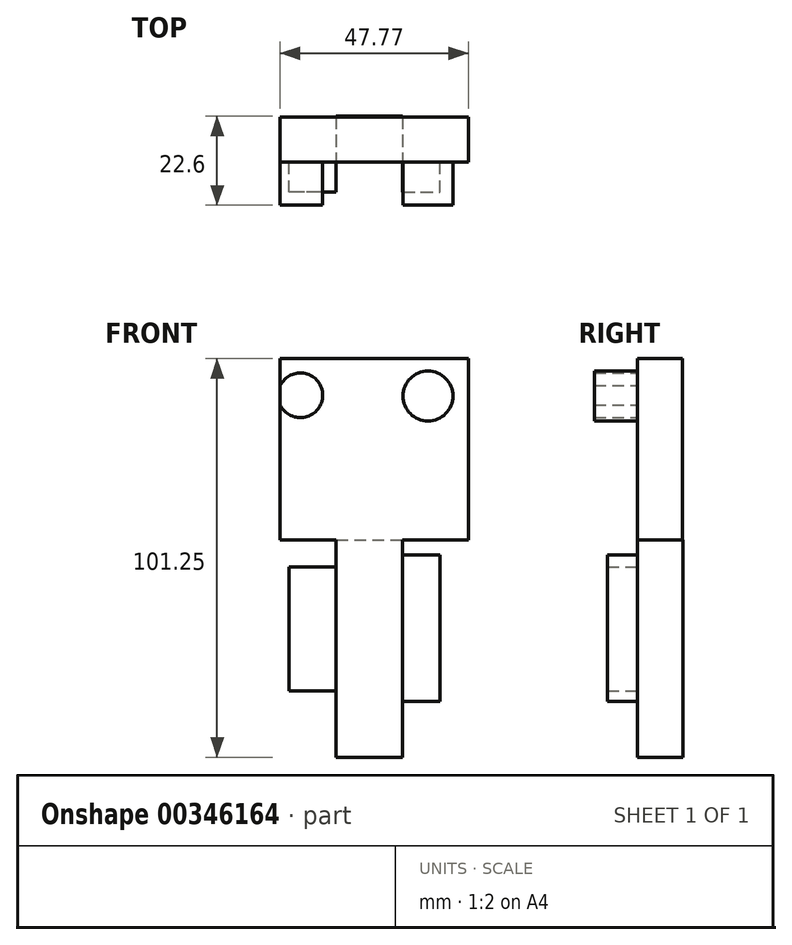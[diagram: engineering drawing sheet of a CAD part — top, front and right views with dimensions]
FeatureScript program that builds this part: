
annotation { "Feature Type Name" : "Feature", "Feature Type Description" : "" }
export const myFeature = defineFeature(function(context is Context, id is Id, definition is map)
    precondition{}
    {
        {
            var Q0;
            Q0=qCreatedBy(makeId("Front.planeOp"),FACE);
            var sketch = newSketch(context, id + "F0", { "sketchPlane" : qUnion([Q0])});
            skLineSegment(sketch, "E0.bottom", {"start": v(-59.34, 47.59) * mm, "end": v(-11.57, 47.59) * mm});
            skLineSegment(sketch, "E0.top", {"start": v(-59.34, 1.52) * mm, "end": v(-11.57, 1.52) * mm});
            skLineSegment(sketch, "E0.left", {"start": v(-59.34, 47.59) * mm, "end": v(-59.34, 1.52) * mm});
            skLineSegment(sketch, "E0.right", {"start": v(-11.57, 47.59) * mm, "end": v(-11.57, 1.52) * mm});
            skSolve(sketch);
        }
        {
            var Q0;
            Q0=makeQuery(id+"F0.imprint","IMPRINT",FACE,{"disambiguationData":[TD([[makeQuery(id+"F0.imprint","IMPRINT",EDGE,{"derivedFrom":sQuery(id+"F0.wireOp",EDGE,"E0.bottom")}),-1.0]])]});
            extrude(context, id + "F1", {"entities" : qUnion([Q0]), "depth" : 11.43 * mm});
        }
        {
            var Q0;
            Q0=makeQuery(id+"F1.opExtrude","CAP_FACE",FACE,{"disambiguationData":[OSD([sQuery(id+"F0.wireOp",EDGE,"E0.bottom"),sQuery(id+"F0.wireOp",EDGE,"E0.top"),sQuery(id+"F0.wireOp",EDGE,"E0.left"),sQuery(id+"F0.wireOp",EDGE,"E0.right")])],"isStart":false});
            var sketch = newSketch(context, id + "F2", { "sketchPlane" : qUnion([Q0])});
            skCircle(sketch, "E1", {"center": v(-54.22, 38.3) * mm, "radius": 5.68 * mm});
            skCircle(sketch, "E2", {"center": v(-21.8, 38.1) * mm, "radius": 6.34 * mm});
            skSolve(sketch);
        }
        {
            var Q0;
            Q0=makeQuery(id+"F2.imprint","IMPRINT",FACE,{"disambiguationData":[TD([[makeQuery(id+"F2.imprint","IMPRINT",EDGE,{"derivedFrom":sQuery(id+"F2.wireOp",EDGE,"E2")}),1.0]])]});
            var Q1;
            {var subQ0=sQuery(id+"F2.wireOp",EDGE,"E1");var subQ1=makeQuery(id+"F1.opExtrude","CAP_EDGE",EDGE,{"disambiguationData":[OSD([sQuery(id+"F0.wireOp",EDGE,"E0.left")])],"isStart":false});var subQ2=makeQuery(id+"F2.imprint","INTERSECT",VERTEX,{"disambiguationData":[OD(0.0)],"derivedFrom":[subQ1,subQ0]});Q1=makeQuery(id+"F2.imprint","IMPRINT",FACE,{"disambiguationData":[TD([[makeQuery(id+"F2.imprint","IMPRINT",EDGE,{"disambiguationData":[TD([[subQ2,1.0]])],"derivedFrom":subQ0}),1.0]])]});}
            extrude(context, id + "F3", {"entities" : qUnion([Q0, Q1]), "operationType" : NewBodyOperationType.ADD, "depth" : 10.92 * mm});
        }
        {
            var Q0;
            Q0=makeQuery(id+"F1.opExtrude","CAP_FACE",FACE,{"disambiguationData":[OSD([sQuery(id+"F0.wireOp",EDGE,"E0.bottom"),sQuery(id+"F0.wireOp",EDGE,"E0.top"),sQuery(id+"F0.wireOp",EDGE,"E0.left"),sQuery(id+"F0.wireOp",EDGE,"E0.right")])],"isStart":false});
            var sketch = newSketch(context, id + "F4", { "sketchPlane" : qUnion([Q0])});
            skLineSegment(sketch, "E3.bottom", {"start": v(-45.12, 1.52) * mm, "end": v(-28.25, 1.52) * mm});
            skLineSegment(sketch, "E3.top", {"start": v(-45.12, -53.66) * mm, "end": v(-28.25, -53.66) * mm});
            skLineSegment(sketch, "E3.left", {"start": v(-45.12, 1.52) * mm, "end": v(-45.12, -53.66) * mm});
            skLineSegment(sketch, "E3.right", {"start": v(-28.25, 1.52) * mm, "end": v(-28.25, -53.66) * mm});
            skSolve(sketch);
        }
        {
            var Q0;
            Q0=makeQuery(id+"F4.imprint","IMPRINT",FACE,{"disambiguationData":[TD([[makeQuery(id+"F4.imprint","IMPRINT",EDGE,{"derivedFrom":sQuery(id+"F4.wireOp",EDGE,"E3.bottom")}),-1.0]])]});
            extrude(context, id + "F5", {"entities" : qUnion([Q0]), "operationType" : NewBodyOperationType.ADD, "oppositeDirection" : true, "depth" : 11.68 * mm});
        }
        {
            var Q0;
            Q0=makeQuery(id+"F5.boolean.opBoolean","MERGE",FACE,{"derivedFrom":[makeQuery(id+"F1.opExtrude","CAP_FACE",FACE,{"disambiguationData":[OSD([sQuery(id+"F0.wireOp",EDGE,"E0.bottom"),sQuery(id+"F0.wireOp",EDGE,"E0.top"),sQuery(id+"F0.wireOp",EDGE,"E0.left"),sQuery(id+"F0.wireOp",EDGE,"E0.right")])],"isStart":false}),makeQuery(id+"F5.opExtrude","CAP_FACE",FACE,{"disambiguationData":[OSD([sQuery(id+"F4.wireOp",EDGE,"E3.bottom"),sQuery(id+"F4.wireOp",EDGE,"E3.top"),sQuery(id+"F4.wireOp",EDGE,"E3.left"),sQuery(id+"F4.wireOp",EDGE,"E3.right")])],"isStart":true})]});
            var sketch = newSketch(context, id + "F6", { "sketchPlane" : qUnion([Q0])});
            skLineSegment(sketch, "E4.bottom", {"start": v(-28.25, -2.28) * mm, "end": v(-18.77, -2.28) * mm});
            skLineSegment(sketch, "E4.top", {"start": v(-28.25, -39.44) * mm, "end": v(-18.77, -39.44) * mm});
            skLineSegment(sketch, "E4.left", {"start": v(-28.25, -2.28) * mm, "end": v(-28.25, -39.44) * mm});
            skLineSegment(sketch, "E4.right", {"start": v(-18.77, -2.28) * mm, "end": v(-18.77, -39.44) * mm});
            skLineSegment(sketch, "E5.bottom", {"start": v(-45.12, -5.3) * mm, "end": v(-57.07, -5.3) * mm});
            skLineSegment(sketch, "E5.top", {"start": v(-45.12, -36.78) * mm, "end": v(-57.07, -36.78) * mm});
            skLineSegment(sketch, "E5.left", {"start": v(-45.12, -5.3) * mm, "end": v(-45.12, -36.78) * mm});
            skLineSegment(sketch, "E5.right", {"start": v(-57.07, -5.3) * mm, "end": v(-57.07, -36.78) * mm});
            skSolve(sketch);
        }
        {
            var Q0;
            Q0=makeQuery(id+"F6.imprint","IMPRINT",FACE,{"disambiguationData":[TD([[makeQuery(id+"F6.imprint","IMPRINT",EDGE,{"derivedFrom":sQuery(id+"F6.wireOp",EDGE,"E5.bottom")}),1.0]])]});
            var Q1;
            Q1=makeQuery(id+"F6.imprint","IMPRINT",FACE,{"disambiguationData":[TD([[makeQuery(id+"F6.imprint","IMPRINT",EDGE,{"derivedFrom":sQuery(id+"F6.wireOp",EDGE,"E4.bottom")}),-1.0]])]});
            extrude(context, id + "F7", {"entities" : qUnion([Q0, Q1]), "depth" : 7.62 * mm});
        }
    });
